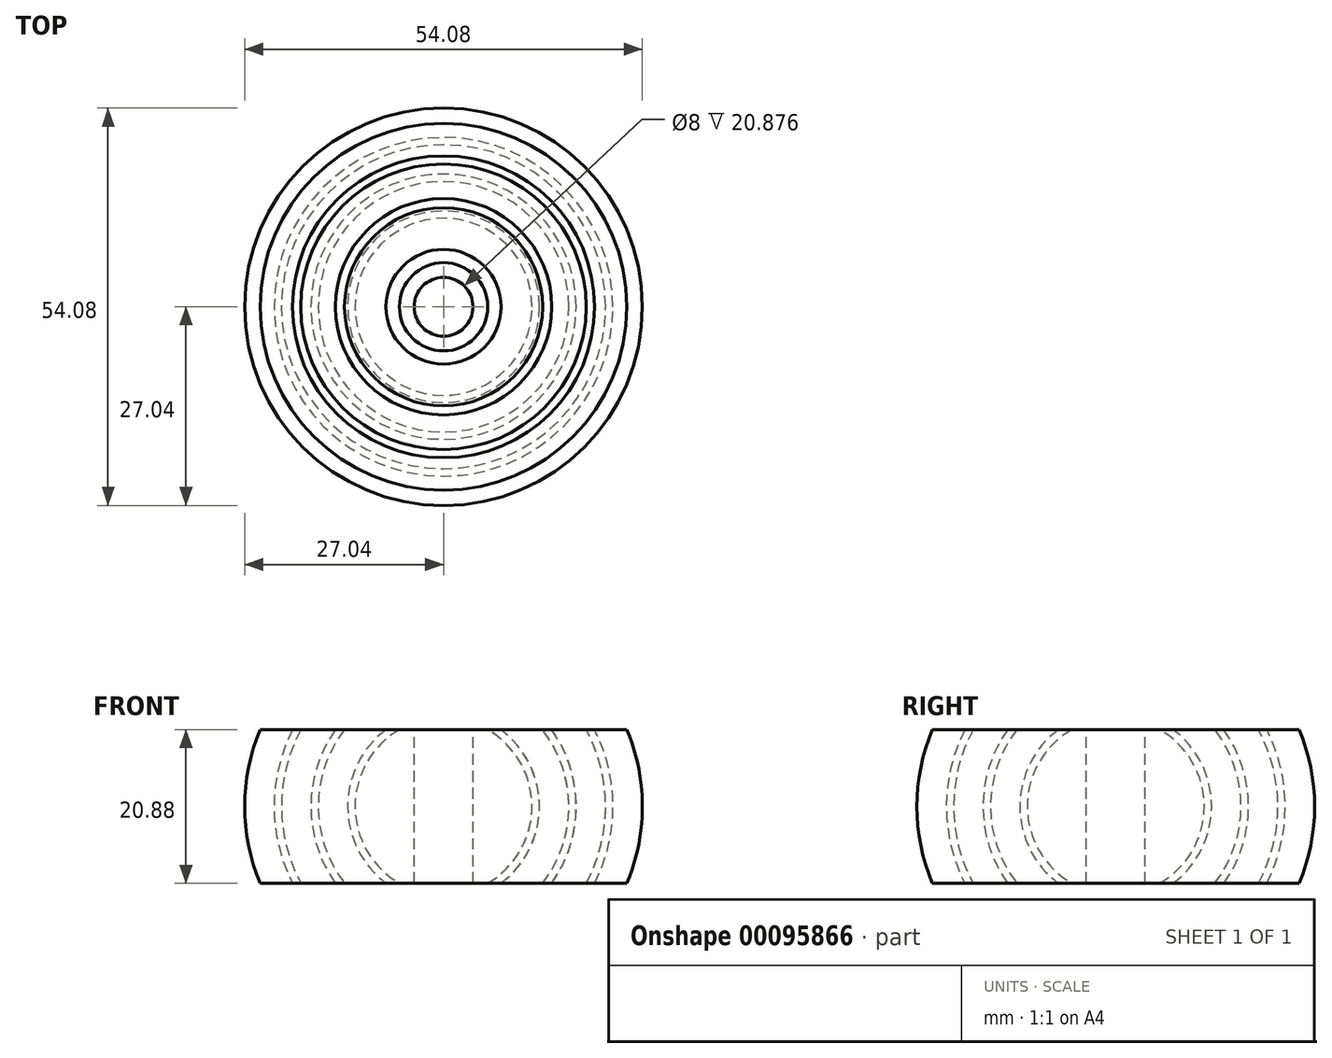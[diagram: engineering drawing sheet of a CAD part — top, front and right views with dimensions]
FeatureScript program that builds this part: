
annotation { "Feature Type Name" : "Feature", "Feature Type Description" : "" }
export const myFeature = defineFeature(function(context is Context, id is Id, definition is map)
    precondition{}
    {
        {
            var Q0;
            Q0=qCreatedBy(makeId("Front.planeOp"),FACE);
            var sketch = newSketch(context, id + "F0", { "sketchPlane" : qUnion([Q0])});
            skCircle(sketch, "E0", {"center": v(0, 0) * mm, "radius": 12.04 * mm});
            skCircle(sketch, "E1", {"center": v(0, 0) * mm, "radius": 13.04 * mm});
            skCircle(sketch, "E2", {"center": v(0, 0) * mm, "radius": 17.04 * mm});
            skCircle(sketch, "E3", {"center": v(0, 0) * mm, "radius": 18.04 * mm});
            skCircle(sketch, "E4", {"center": v(0, 0) * mm, "radius": 22.04 * mm});
            skCircle(sketch, "E5", {"center": v(0, 0) * mm, "radius": 23.04 * mm});
            skCircle(sketch, "E6", {"center": v(0, 0) * mm, "radius": 27.04 * mm});
            skLineSegment(sketch, "E7", {"start": v(-24.94, 10.44) * mm, "end": v(24.94, 10.44) * mm});
            skLineSegment(sketch, "E8", {"start": v(0, 27.04) * mm, "end": v(0, -27.04) * mm});
            skPoint(sketch, "E9", {"position": v(-20.54, 10.44) * mm});
            skPoint(sketch, "E10", {"position": v(-22.04, 0) * mm});
            skLineSegment(sketch, "E11.MirrorCS", {"start": v(-24.94, -10.44) * mm, "end": v(24.94, -10.44) * mm});
            skLineSegment(sketch, "E12", {"start": v(-4, 10.44) * mm, "end": v(-4, -10.44) * mm});
            skPoint(sketch, "E13", {"position": v(-6, 10.44) * mm});
            skSolve(sketch);
        }
        {
            var Q0;
            {var subQ0=sQuery(id+"F0.wireOp",EDGE,"E7");var subQ1=sQuery(id+"F0.wireOp",EDGE,"E1");var subQ2=makeQuery(id+"F0.imprint","INTERSECT",VERTEX,{"disambiguationData":[OD(1.0)],"derivedFrom":[subQ1,subQ0]});Q0=makeQuery(id+"F0.imprint","IMPRINT",FACE,{"disambiguationData":[TD([[makeQuery(id+"F0.imprint","IMPRINT",EDGE,{"disambiguationData":[TD([[subQ2,-1.0]])],"derivedFrom":subQ1}),-1.0]])]});}
            var Q1;
            {var subQ0=sQuery(id+"F0.wireOp",EDGE,"E7");var subQ1=sQuery(id+"F0.wireOp",EDGE,"E3");var subQ2=makeQuery(id+"F0.imprint","INTERSECT",VERTEX,{"disambiguationData":[OD(1.0)],"derivedFrom":[subQ1,subQ0]});Q1=makeQuery(id+"F0.imprint","IMPRINT",FACE,{"disambiguationData":[TD([[makeQuery(id+"F0.imprint","IMPRINT",EDGE,{"disambiguationData":[TD([[subQ2,-1.0]])],"derivedFrom":subQ1}),-1.0]])]});}
            var Q2;
            {var subQ0=sQuery(id+"F0.wireOp",EDGE,"E7");var subQ1=sQuery(id+"F0.wireOp",EDGE,"E5");var subQ2=makeQuery(id+"F0.imprint","INTERSECT",VERTEX,{"disambiguationData":[OD(1.0)],"derivedFrom":[subQ1,subQ0]});Q2=makeQuery(id+"F0.imprint","IMPRINT",FACE,{"disambiguationData":[TD([[makeQuery(id+"F0.imprint","IMPRINT",EDGE,{"disambiguationData":[TD([[subQ2,-1.0]])],"derivedFrom":subQ1}),-1.0]])]});}
            var Q3;
            {var subQ5=sQuery(id+"F0.wireOp",EDGE,"E12");Q3=makeQuery(id+"F0.imprint","IMPRINT",FACE,{"disambiguationData":[TD([[makeQuery(id+"F0.imprint","IMPRINT",EDGE,{"derivedFrom":subQ5}),-1.0]])]});}
            var Q4;
            Q4=sQuery(id+"F0.wireOp",EDGE,"E8");
            revolve(context, id + "F1", {"entities" : qUnion([Q0, Q1, Q2, Q3]), "axis" : qUnion([Q4]), "revolveType" : RevolveType.FULL});
        }
    });
